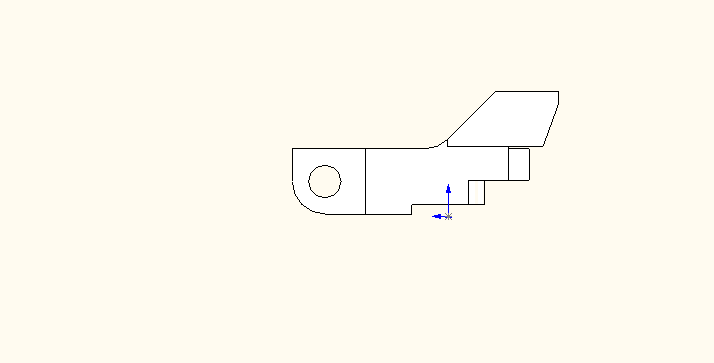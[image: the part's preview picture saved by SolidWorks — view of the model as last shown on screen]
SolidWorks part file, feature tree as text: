
SOLIDWORKS PART (.sldprt)
format: sldprt  version: not decoded by parser v0  size: 660,480 bytes
history: native  units: mm
features: sketch x11, cut_extrude x9, extrude x2, fillet x2, material x1, plane x1 (+11 scaffold rows collapsed)
feature tree (37):
  scaffold x11  (default folders/planes/origin — collapsed)
  material  "6061 Alloy"
  plane  "CenterPlane"  Offset=0mm
  sketch  "SolidS"  dims[D1=1.5875mm D2=1.5875mm D3=0.0mm D4=0.0mm D5=0.0mm]
  extrude  "Solid"  Depth=0mm
  sketch  "Sketch3"  dims[c1.D1=1.6919mm c2.D1=0.0deg c2.D2=0.0mm c2.D3=0.0508mm c3.D1=0.0508mm c3.D3=3.302mm c4.D3=100.0deg c4.D1=1.778mm]
  cut_extrude  "Outer Clamp Clearance"  Depth=12.7mm
  sketch  "Sketch4"  dims[D1=2.159mm D2=0.0mm]
  cut_extrude  "Latch Clearance"  [1 undecoded]
  fillet  "Fillet1"  Radius=0.79375mm
  sketch  "Sketch7"  dims[D1=0.0508mm D2=2.54mm D3=2.9464mm D4=3.556mm]
  cut_extrude  "Cut-Extrude4"  [1 undecoded]
  sketch  "Sketch8"  dims[D1=1.016mm D2=2.159mm D3=0.762mm]
  cut_extrude  "Cut-Extrude5"  Depth=2.54mm
  sketch  "Sketch9"  dims[D1=2.3622mm D2=1.7526mm D3=2.54mm]
  cut_extrude  "Cut-Extrude6"  [1 undecoded]
  sketch  "Sketch10"  dims[c1.D1=~4.607539mm c2.D1=45.0deg c2.D2=1.524mm c2.D3=1.27mm c2.D4=1.27mm c2.D5=0.635mm c3.D4=1.27mm c3.D6=1.016mm c3.D2=4.445mm c3.D3=2.794mm c4.D4=~3.055323mm c5.D4=70.0deg c5.D5=5.08mm]
  extrude  "Extrude2"  Depth=1.905mm
  fillet  "Fillet2"  Radius=1.5875mm
  sketch  "Sketch11"  dims[c1.D1=11.43mm c1.D2=1.524mm c2.D1=0.127mm c2.D3=1.5875mm]
  cut_extrude  "Cut-Extrude8"  Depth=1.016mm
  sketch  "Sketch13"
  cut_extrude  "Cut-Extrude9"  Depth=2.54mm
  sketch  "Sketch14"  dims[D1=0.635mm]
  cut_extrude  "Cut-Extrude10"  [1 undecoded]
  sketch  "Sketch15"
  cut_extrude  "Cut-Extrude11"  Depth=0.127mm
decode coverage: 18 of 24 modeling features carry decoded parameters
note: ~ marks probable driven/reference dimensions
note: 4 parameter values undecoded
summary: no parameter record found for 4 features
note: suppression state not decoded; provenance and decode notes live in map.json
